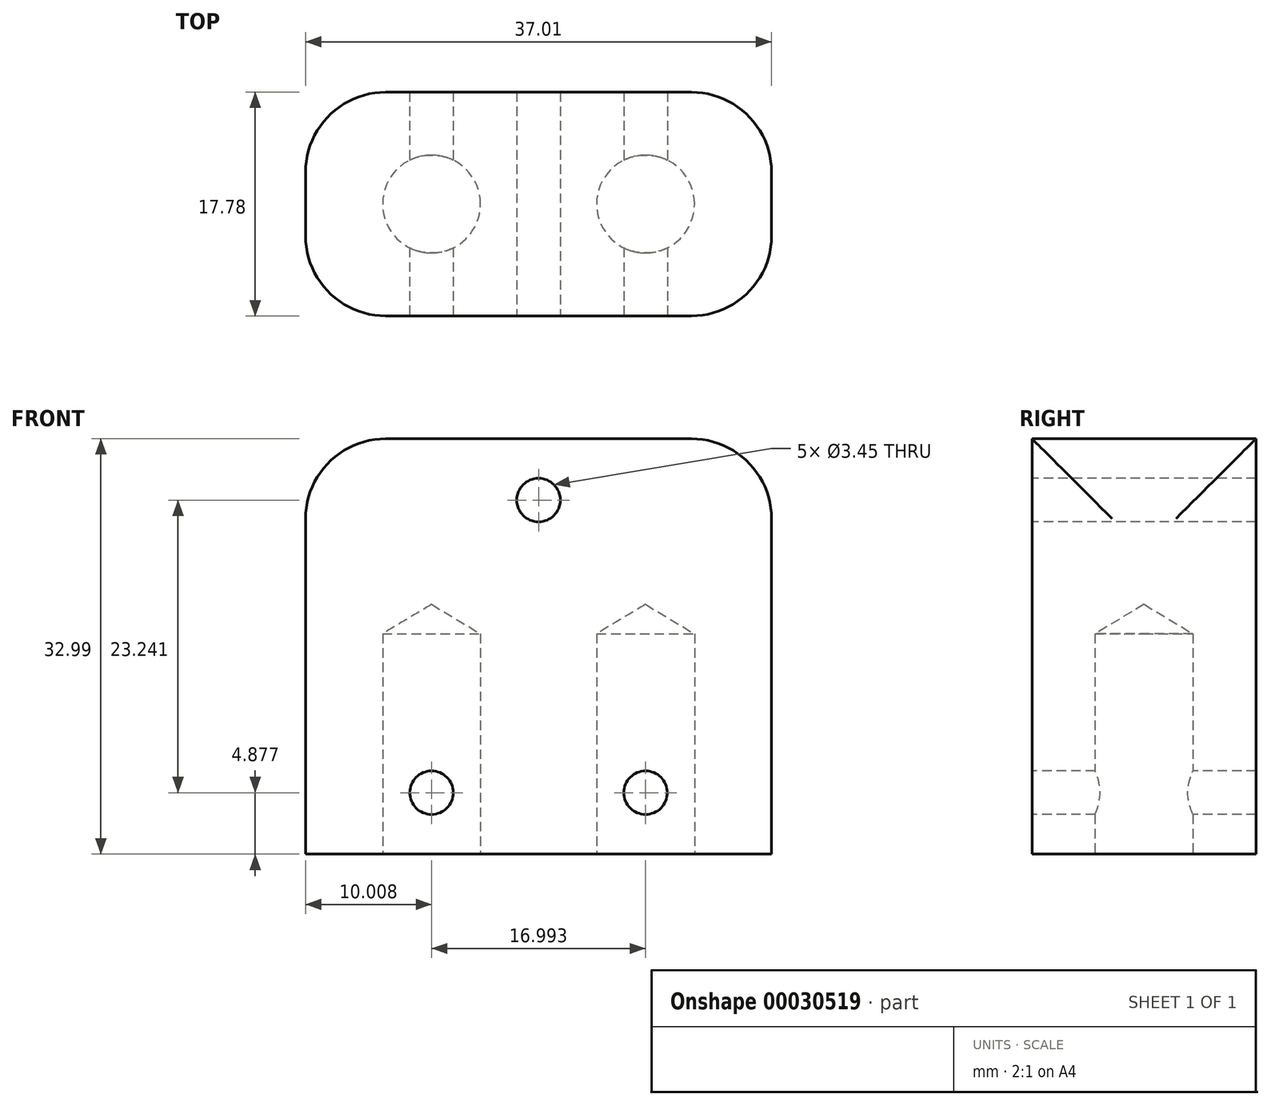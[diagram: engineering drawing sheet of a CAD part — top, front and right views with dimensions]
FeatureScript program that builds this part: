
annotation { "Feature Type Name" : "Feature", "Feature Type Description" : "" }
export const myFeature = defineFeature(function(context is Context, id is Id, definition is map)
    precondition{}
    {
        {
            var Q0;
            Q0=qCreatedBy(makeId("Front.planeOp"),FACE);
            var sketch = newSketch(context, id + "F0", { "sketchPlane" : qUnion([Q0])});
            skLineSegment(sketch, "E0.bottom", {"start": v(0, 0) * mm, "end": v(37, 0) * mm});
            skLineSegment(sketch, "E0.top", {"start": v(0, 33) * mm, "end": v(37, 33) * mm});
            skLineSegment(sketch, "E0.left", {"start": v(0, 0) * mm, "end": v(0, 33) * mm});
            skLineSegment(sketch, "E0.right", {"start": v(37, 0) * mm, "end": v(37, 33) * mm});
            skSolve(sketch);
        }
        {
            var Q0;
            Q0=makeQuery(id+"F0.imprint","IMPRINT",FACE,{"disambiguationData":[TD([[makeQuery(id+"F0.imprint","IMPRINT",EDGE,{"derivedFrom":sQuery(id+"F0.wireOp",EDGE,"E0.bottom")}),1.0]])]});
            extrude(context, id + "F1", {"entities" : qUnion([Q0]), "depth" : 17.78 * mm});
        }
        {
            var Q0;
            Q0=makeQuery(id+"F1.opExtrude","SWEPT_FACE",FACE,{"disambiguationData":[OSD([sQuery(id+"F0.wireOp",EDGE,"E0.top")])]});
            var sketch = newSketch(context, id + "F2", { "sketchPlane" : qUnion([Q0])});
            skLineSegment(sketch, "E1", {"start": v(0, -8.9) * mm, "end": v(37, -8.9) * mm, "construction": true});
            skLineSegment(sketch, "E2", {"start": v(18.5, 0) * mm, "end": v(18.5, -17.78) * mm, "construction": true});
            skPoint(sketch, "E3", {"position": v(18.5, -8.9) * mm});
            skSolve(sketch);
        }
        {
            var Q0;
            Q0=makeQuery(id+"F1.opExtrude","SWEPT_FACE",FACE,{"disambiguationData":[OSD([sQuery(id+"F0.wireOp",EDGE,"E0.bottom")])]});
            var sketch = newSketch(context, id + "F3", { "sketchPlane" : qUnion([Q0])});
            skPoint(sketch, "E4", {"position": v(10, 8.89) * mm});
            skPoint(sketch, "E5", {"position": v(27, 8.9) * mm});
            skSolve(sketch);
        }
        {
            var Q0;
            Q0=sQuery(id+"F3.wireOp",VERTEX,"E4");
            var Q1;
            Q1=sQuery(id+"F3.wireOp",VERTEX,"E5");
            var Q2;
            Q2=makeQuery(id+"F1.opExtrude","SWEPT_BODY",BODY,{"disambiguationData":[OSD([sQuery(id+"F0.wireOp",EDGE,"E0.bottom"),sQuery(id+"F0.wireOp",EDGE,"E0.top"),sQuery(id+"F0.wireOp",EDGE,"E0.left"),sQuery(id+"F0.wireOp",EDGE,"E0.right")])]});
            hole(context, id + "F4", {"style" : HoleStyle.SIMPLE, "holeDiameter" : 7.77 * mm, "endStyle" : HoleEndStyle.BLIND, "holeDepth" : 17.5 * mm, "locations" : qUnion([Q0, Q1]), "scope" : qUnion([Q2])});
        }
        {
            var Q0;
            Q0=makeQuery(id+"F1.opExtrude","SWEPT_EDGE",EDGE,{"disambiguationData":[OSD([sQuery(id+"F0.wireOp",EDGE,"E0.top"),sQuery(id+"F0.wireOp",EDGE,"E0.right")])]});
            var Q1;
            Q1=makeQuery(id+"F1.opExtrude","SWEPT_EDGE",EDGE,{"disambiguationData":[OSD([sQuery(id+"F0.wireOp",EDGE,"E0.top"),sQuery(id+"F0.wireOp",EDGE,"E0.left")])]});
            fillet(context, id + "F5", {"entities" : qUnion([Q0, Q1]), "radius" : 6.35 * mm, "tangentPropagation" : true, "allowEdgeOverflow" : false});
        }
        {
            var Q0;
            Q0=makeQuery(id+"F1.opExtrude","CAP_EDGE",EDGE,{"disambiguationData":[OSD([sQuery(id+"F0.wireOp",EDGE,"E0.right")])],"isStart":false});
            var Q1;
            Q1=makeQuery(id+"F1.opExtrude","CAP_EDGE",EDGE,{"disambiguationData":[OSD([sQuery(id+"F0.wireOp",EDGE,"E0.right")])],"isStart":true});
            var Q2;
            Q2=makeQuery(id+"F1.opExtrude","CAP_EDGE",EDGE,{"disambiguationData":[OSD([sQuery(id+"F0.wireOp",EDGE,"E0.left")])],"isStart":false});
            var Q3;
            Q3=makeQuery(id+"F1.opExtrude","CAP_EDGE",EDGE,{"disambiguationData":[OSD([sQuery(id+"F0.wireOp",EDGE,"E0.left")])],"isStart":true});
            fillet(context, id + "F6", {"entities" : qUnion([Q0, Q1, Q2, Q3]), "radius" : 6.35 * mm, "allowEdgeOverflow" : false});
        }
        {
            var Q0;
            Q0=makeQuery(id+"F1.opExtrude","CAP_FACE",FACE,{"disambiguationData":[OSD([sQuery(id+"F0.wireOp",EDGE,"E0.bottom"),sQuery(id+"F0.wireOp",EDGE,"E0.top"),sQuery(id+"F0.wireOp",EDGE,"E0.left"),sQuery(id+"F0.wireOp",EDGE,"E0.right")])],"isStart":false});
            var sketch = newSketch(context, id + "F7", { "sketchPlane" : qUnion([Q0])});
            skPoint(sketch, "E6", {"position": v(18.5, 28.12) * mm});
            skPoint(sketch, "E7", {"position": v(10, 4.88) * mm});
            skPoint(sketch, "E8", {"position": v(27, 4.88) * mm});
            skSolve(sketch);
        }
        {
            var Q0;
            Q0=sQuery(id+"F7.wireOp",VERTEX,"E6");
            var Q1;
            Q1=sQuery(id+"F7.wireOp",VERTEX,"E7");
            var Q2;
            Q2=sQuery(id+"F7.wireOp",VERTEX,"E8");
            var Q3;
            Q3=makeQuery(id+"F1.opExtrude","SWEPT_BODY",BODY,{"disambiguationData":[OSD([sQuery(id+"F0.wireOp",EDGE,"E0.bottom"),sQuery(id+"F0.wireOp",EDGE,"E0.top"),sQuery(id+"F0.wireOp",EDGE,"E0.left"),sQuery(id+"F0.wireOp",EDGE,"E0.right")])]});
            hole(context, id + "F8", {"style" : HoleStyle.SIMPLE, "holeDiameter" : 3.45 * mm, "endStyle" : HoleEndStyle.THROUGH, "locations" : qUnion([Q0, Q1, Q2]), "scope" : qUnion([Q3]), "standardTappedOrClearance" : lookupTablePath({ "standard" : "ANSI", "engagement" : "75%", "pitch" : "32 tpi", "size" : "#8", "type" : "Tapped" }), "standardBlindInLast" : lookupTablePath({ "standard" : "ANSI", "engagement" : "75%", "pitch" : "32 tpi", "size" : "#8", "type" : "Tapped" }), "isTappedThrough" : true, "majorDiameter" : 4.17 * mm, "showTappedDepth" : true});
        }
    });
